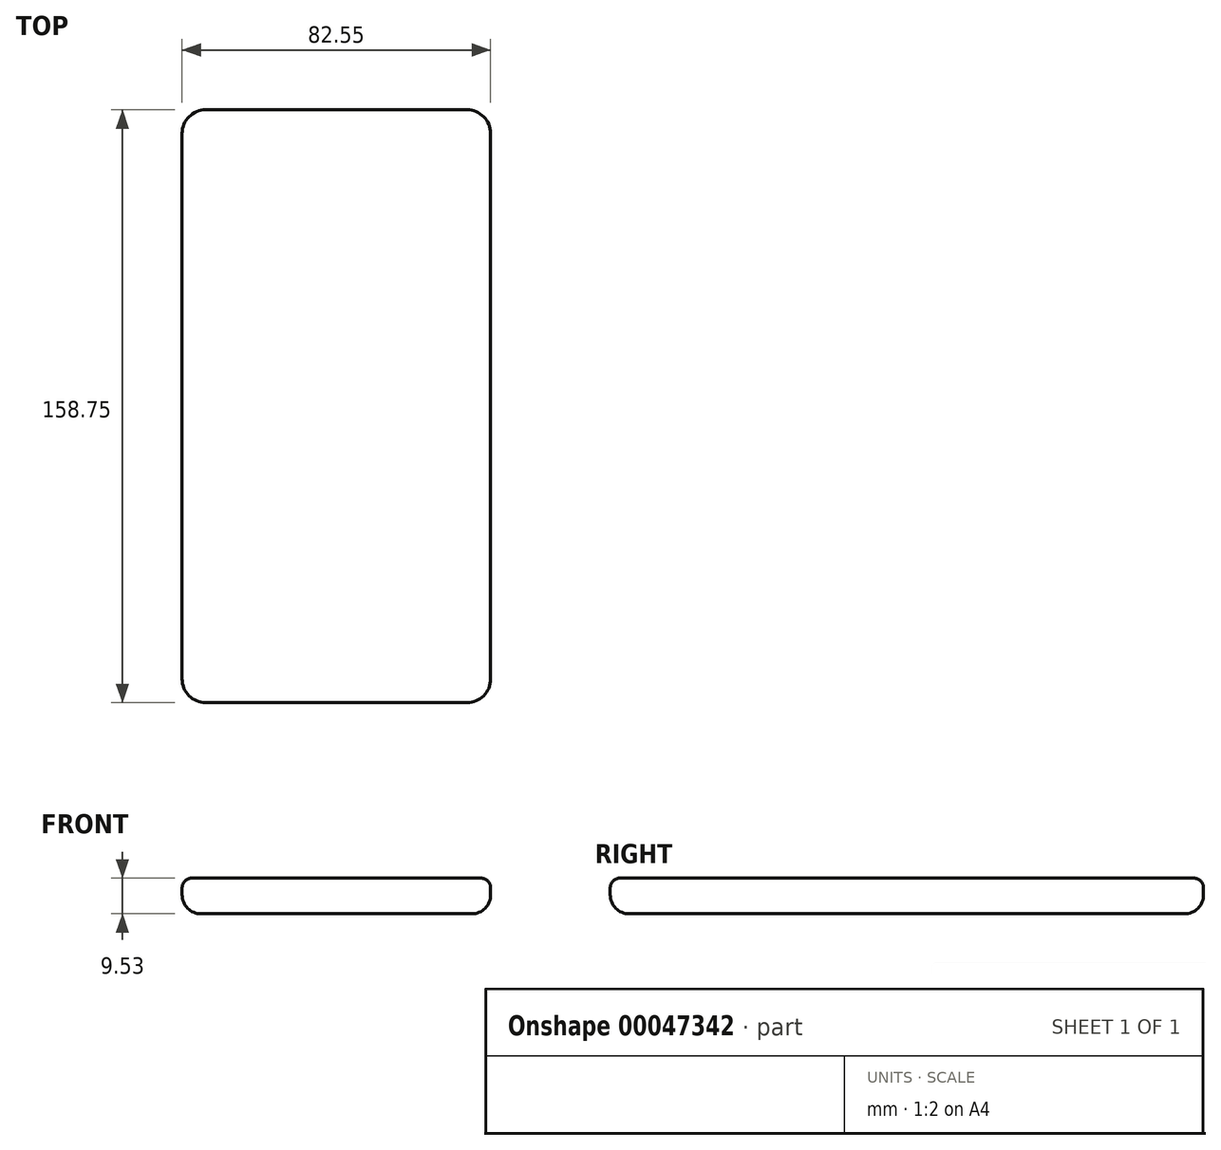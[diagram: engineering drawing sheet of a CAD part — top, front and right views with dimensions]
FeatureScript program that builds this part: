
annotation { "Feature Type Name" : "Feature", "Feature Type Description" : "" }
export const myFeature = defineFeature(function(context is Context, id is Id, definition is map)
    precondition{}
    {
        {
            var Q0;
            Q0=qCreatedBy(makeId("Top.planeOp"),FACE);
            var sketch = newSketch(context, id + "F0", { "sketchPlane" : qUnion([Q0])});
            skLineSegment(sketch, "E0.bottom", {"start": v(-35.74, 89.69) * mm, "end": v(34.1, 89.69) * mm});
            skLineSegment(sketch, "E0.top", {"start": v(-35.74, -69.06) * mm, "end": v(34.1, -69.06) * mm});
            skLineSegment(sketch, "E0.left", {"start": v(-42.1, 83.34) * mm, "end": v(-42.1, -62.71) * mm});
            skLineSegment(sketch, "E0.right", {"start": v(40.46, 83.34) * mm, "end": v(40.46, -62.71) * mm});
            skPoint(sketch, "E1.visualSharp", {"position": v(-42.1, 89.69) * mm});
            skArc(sketch, "E1.filletArc", {"start": v(-35.74, 89.69) * mm, "mid": v(-40.23, 87.83) * mm, "end": v(-42.1, 83.34) * mm});
            skPoint(sketch, "E2.visualSharp", {"position": v(40.46, 89.69) * mm});
            skArc(sketch, "E2.filletArc", {"start": v(40.46, 83.34) * mm, "mid": v(38.6, 87.83) * mm, "end": v(34.1, 89.69) * mm});
            skPoint(sketch, "E3.visualSharp", {"position": v(40.46, -69.06) * mm});
            skArc(sketch, "E3.filletArc", {"start": v(34.1, -69.06) * mm, "mid": v(38.6, -67.2) * mm, "end": v(40.46, -62.71) * mm});
            skPoint(sketch, "E4.visualSharp", {"position": v(-42.1, -69.06) * mm});
            skArc(sketch, "E4.filletArc", {"start": v(-42.1, -62.71) * mm, "mid": v(-40.23, -67.2) * mm, "end": v(-35.74, -69.06) * mm});
            skSolve(sketch);
        }
        {
            var Q0;
            Q0 = qSketchRegion(id + "F0", true);
            extrude(context, id + "F1", {"entities" : qUnion([Q0]), "depth" : 9.52 * mm});
        }
        {
            var Q0;
            Q0=makeQuery(id+"F1.opExtrude","CAP_EDGE",EDGE,{"disambiguationData":[OSD([sQuery(id+"F0.wireOp",EDGE,"E0.left")])],"isStart":false});
            var Q1;
            Q1=makeQuery(id+"F1.opExtrude","CAP_EDGE",EDGE,{"disambiguationData":[OSD([sQuery(id+"F0.wireOp",EDGE,"E4.filletArc")])],"isStart":false});
            var Q2;
            Q2=makeQuery(id+"F1.opExtrude","CAP_EDGE",EDGE,{"disambiguationData":[OSD([sQuery(id+"F0.wireOp",EDGE,"E0.top")])],"isStart":false});
            var Q3;
            Q3=makeQuery(id+"F1.opExtrude","CAP_EDGE",EDGE,{"disambiguationData":[OSD([sQuery(id+"F0.wireOp",EDGE,"E3.filletArc")])],"isStart":false});
            var Q4;
            Q4=makeQuery(id+"F1.opExtrude","CAP_EDGE",EDGE,{"disambiguationData":[OSD([sQuery(id+"F0.wireOp",EDGE,"E0.right")])],"isStart":false});
            var Q5;
            Q5=makeQuery(id+"F1.opExtrude","CAP_EDGE",EDGE,{"disambiguationData":[OSD([sQuery(id+"F0.wireOp",EDGE,"E2.filletArc")])],"isStart":false});
            var Q6;
            Q6=makeQuery(id+"F1.opExtrude","CAP_EDGE",EDGE,{"disambiguationData":[OSD([sQuery(id+"F0.wireOp",EDGE,"E0.bottom")])],"isStart":false});
            var Q7;
            Q7=makeQuery(id+"F1.opExtrude","CAP_EDGE",EDGE,{"disambiguationData":[OSD([sQuery(id+"F0.wireOp",EDGE,"E1.filletArc")])],"isStart":false});
            fillet(context, id + "F2", {"entities" : qUnion([Q0, Q1, Q2, Q3, Q4, Q5, Q6, Q7]), "radius" : 2.54 * mm, "tangentPropagation" : true, "allowEdgeOverflow" : false});
        }
        {
            var Q0;
            Q0=makeQuery(id+"F1.opExtrude","CAP_EDGE",EDGE,{"disambiguationData":[OSD([sQuery(id+"F0.wireOp",EDGE,"E0.left")])],"isStart":true});
            var Q1;
            Q1=makeQuery(id+"F1.opExtrude","CAP_EDGE",EDGE,{"disambiguationData":[OSD([sQuery(id+"F0.wireOp",EDGE,"E4.filletArc")])],"isStart":true});
            var Q2;
            Q2=makeQuery(id+"F1.opExtrude","CAP_EDGE",EDGE,{"disambiguationData":[OSD([sQuery(id+"F0.wireOp",EDGE,"E0.top")])],"isStart":true});
            var Q3;
            Q3=makeQuery(id+"F1.opExtrude","CAP_EDGE",EDGE,{"disambiguationData":[OSD([sQuery(id+"F0.wireOp",EDGE,"E3.filletArc")])],"isStart":true});
            var Q4;
            Q4=makeQuery(id+"F1.opExtrude","CAP_EDGE",EDGE,{"disambiguationData":[OSD([sQuery(id+"F0.wireOp",EDGE,"E0.right")])],"isStart":true});
            var Q5;
            Q5=makeQuery(id+"F1.opExtrude","CAP_EDGE",EDGE,{"disambiguationData":[OSD([sQuery(id+"F0.wireOp",EDGE,"E2.filletArc")])],"isStart":true});
            var Q6;
            Q6=makeQuery(id+"F1.opExtrude","CAP_EDGE",EDGE,{"disambiguationData":[OSD([sQuery(id+"F0.wireOp",EDGE,"E0.bottom")])],"isStart":true});
            var Q7;
            Q7=makeQuery(id+"F1.opExtrude","CAP_EDGE",EDGE,{"disambiguationData":[OSD([sQuery(id+"F0.wireOp",EDGE,"E1.filletArc")])],"isStart":true});
            fillet(context, id + "F3", {"entities" : qUnion([Q0, Q1, Q2, Q3, Q4, Q5, Q6, Q7]), "radius" : 5.08 * mm, "tangentPropagation" : true, "allowEdgeOverflow" : false});
        }
    });
